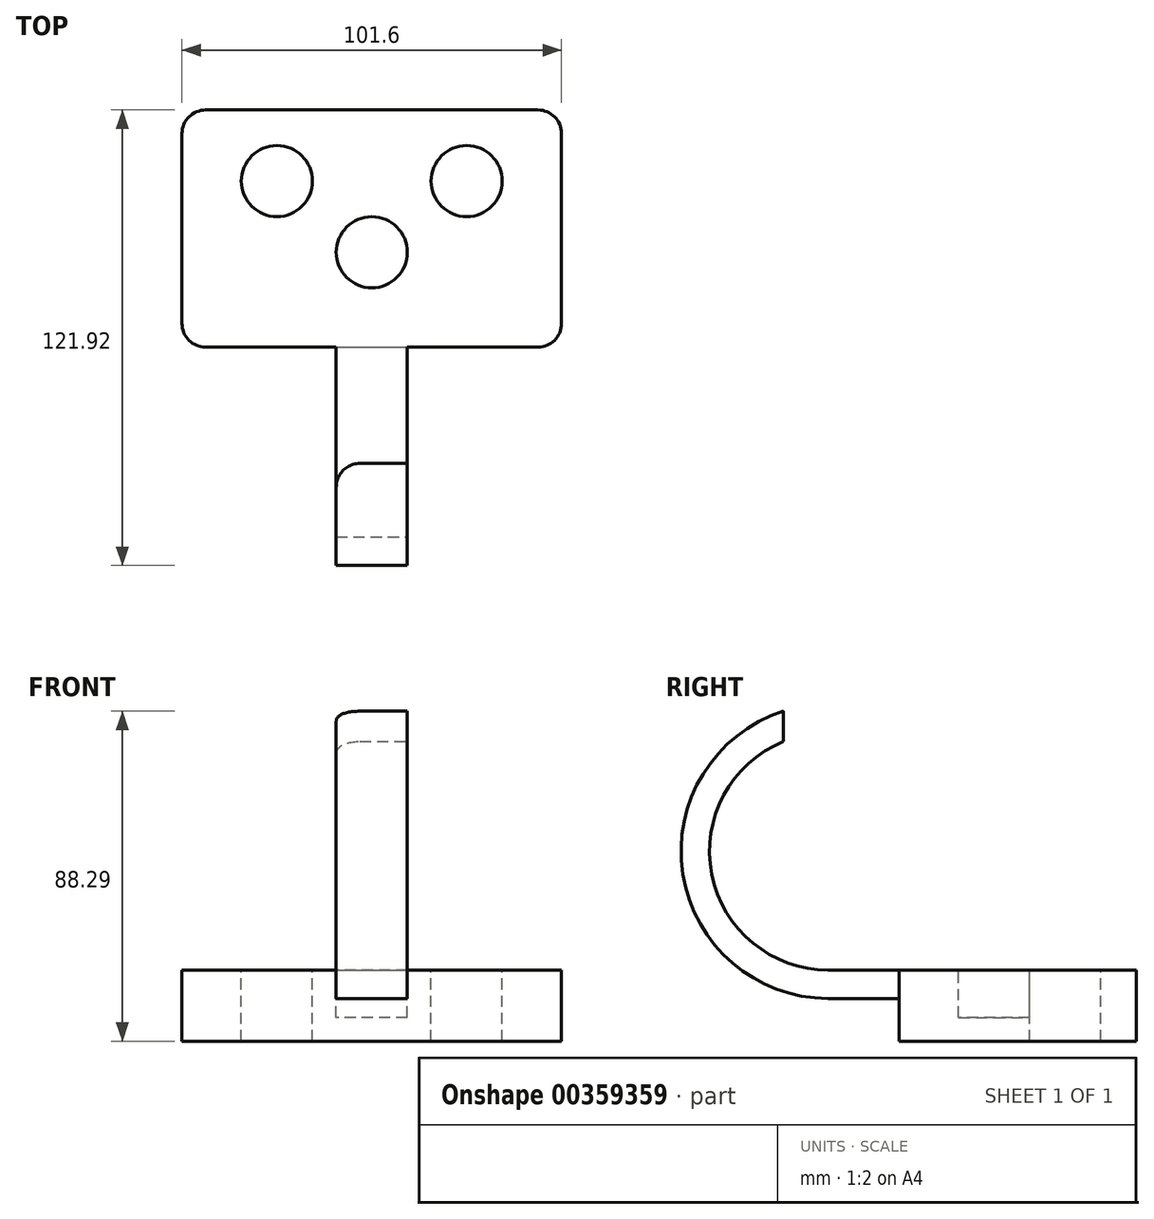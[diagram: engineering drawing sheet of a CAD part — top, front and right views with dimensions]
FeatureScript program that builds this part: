
annotation { "Feature Type Name" : "Feature", "Feature Type Description" : "" }
export const myFeature = defineFeature(function(context is Context, id is Id, definition is map)
    precondition{}
    {
        {
            var Q0;
            Q0=qCreatedBy(makeId("Top.planeOp"),FACE);
            var sketch = newSketch(context, id + "F0", { "sketchPlane" : qUnion([Q0])});
            skLineSegment(sketch, "E0.bottom", {"start": v(0, 0) * mm, "end": v(101.6, 0) * mm});
            skLineSegment(sketch, "E0.top", {"start": v(0, -63.5) * mm, "end": v(101.6, -63.5) * mm});
            skLineSegment(sketch, "E0.left", {"start": v(0, 0) * mm, "end": v(0, -63.5) * mm});
            skLineSegment(sketch, "E0.right", {"start": v(101.6, 0) * mm, "end": v(101.6, -63.5) * mm});
            skSolve(sketch);
        }
        {
            var Q0;
            Q0=makeQuery(id+"F0.imprint","IMPRINT",FACE,{"disambiguationData":[TD([[makeQuery(id+"F0.imprint","IMPRINT",EDGE,{"derivedFrom":sQuery(id+"F0.wireOp",EDGE,"E0.bottom")}),-1.0]])]});
            extrude(context, id + "F1", {"entities" : qUnion([Q0]), "depth" : 19.05 * mm});
        }
        {
            var Q0;
            Q0=makeQuery(id+"F1.opExtrude","SWEPT_EDGE",EDGE,{"disambiguationData":[OSD([sQuery(id+"F0.wireOp",EDGE,"E0.top"),sQuery(id+"F0.wireOp",EDGE,"E0.right")])]});
            var Q1;
            Q1=makeQuery(id+"F1.opExtrude","SWEPT_EDGE",EDGE,{"disambiguationData":[OSD([sQuery(id+"F0.wireOp",EDGE,"E0.bottom"),sQuery(id+"F0.wireOp",EDGE,"E0.right")])]});
            var Q2;
            Q2=makeQuery(id+"F1.opExtrude","SWEPT_EDGE",EDGE,{"disambiguationData":[OSD([sQuery(id+"F0.wireOp",EDGE,"E0.top"),sQuery(id+"F0.wireOp",EDGE,"E0.left")])]});
            var Q3;
            Q3=makeQuery(id+"F1.opExtrude","SWEPT_EDGE",EDGE,{"disambiguationData":[OSD([sQuery(id+"F0.wireOp",EDGE,"E0.bottom"),sQuery(id+"F0.wireOp",EDGE,"E0.left")])]});
            fillet(context, id + "F2", {"entities" : qUnion([Q0, Q1, Q2, Q3]), "radius" : 6.35 * mm, "tangentPropagation" : true, "allowEdgeOverflow" : false});
        }
        {
            var Q0;
            Q0=makeQuery(id+"F1.opExtrude","CAP_FACE",FACE,{"disambiguationData":[OSD([sQuery(id+"F0.wireOp",EDGE,"E0.bottom"),sQuery(id+"F0.wireOp",EDGE,"E0.top"),sQuery(id+"F0.wireOp",EDGE,"E0.left"),sQuery(id+"F0.wireOp",EDGE,"E0.right")])],"isStart":false});
            var sketch = newSketch(context, id + "F3", { "sketchPlane" : qUnion([Q0])});
            skCircle(sketch, "E1", {"center": v(50.8, -38.1) * mm, "radius": 9.53 * mm});
            skPoint(sketch, "E1.centerSnap0", {"position": v(50.8, -63.5) * mm});
            skCircle(sketch, "E2", {"center": v(76.2, -19.05) * mm, "radius": 9.53 * mm});
            skCircle(sketch, "E3", {"center": v(25.4, -19.05) * mm, "radius": 9.53 * mm});
            skSolve(sketch);
        }
        {
            var Q0;
            Q0=makeQuery(id+"F3.imprint","IMPRINT",FACE,{"disambiguationData":[TD([[makeQuery(id+"F3.imprint","IMPRINT",EDGE,{"derivedFrom":sQuery(id+"F3.wireOp",EDGE,"E1")}),1.0]])]});
            extrude(context, id + "F4", {"entities" : qUnion([Q0]), "operationType" : NewBodyOperationType.REMOVE, "oppositeDirection" : true, "depth" : 12.7 * mm});
        }
        {
            var Q0;
            Q0=makeQuery(id+"F3.imprint","IMPRINT",FACE,{"disambiguationData":[TD([[makeQuery(id+"F3.imprint","IMPRINT",EDGE,{"derivedFrom":sQuery(id+"F3.wireOp",EDGE,"E3")}),1.0]])]});
            var Q1;
            Q1=makeQuery(id+"F3.imprint","IMPRINT",FACE,{"disambiguationData":[TD([[makeQuery(id+"F3.imprint","IMPRINT",EDGE,{"derivedFrom":sQuery(id+"F3.wireOp",EDGE,"E2")}),1.0]])]});
            extrude(context, id + "F5", {"entities" : qUnion([Q0, Q1]), "operationType" : NewBodyOperationType.REMOVE, "endBound" : BoundingType.THROUGH_ALL, "oppositeDirection" : true, "depth" : 25.4 * mm});
        }
        {
            var Q0;
            Q0=makeQuery(id+"F1.opExtrude","SWEPT_FACE",FACE,{"disambiguationData":[OSD([sQuery(id+"F0.wireOp",EDGE,"E0.top")])]});
            var sketch = newSketch(context, id + "F6", { "sketchPlane" : qUnion([Q0])});
            skLineSegment(sketch, "E4.bottom", {"start": v(41.28, 19.05) * mm, "end": v(60.33, 19.05) * mm});
            skLineSegment(sketch, "E4.top", {"start": v(41.28, 11.43) * mm, "end": v(60.33, 11.43) * mm});
            skLineSegment(sketch, "E4.left", {"start": v(41.28, 19.05) * mm, "end": v(41.28, 11.43) * mm});
            skLineSegment(sketch, "E4.right", {"start": v(60.33, 19.05) * mm, "end": v(60.33, 11.43) * mm});
            skSolve(sketch);
        }
        {
            var Q0;
            Q0=makeQuery(id+"F6.imprint","IMPRINT",FACE,{"disambiguationData":[TD([[makeQuery(id+"F6.imprint","IMPRINT",EDGE,{"derivedFrom":sQuery(id+"F6.wireOp",EDGE,"E4.bottom")}),-1.0]])]});
            extrude(context, id + "F7", {"entities" : qUnion([Q0]), "operationType" : NewBodyOperationType.ADD, "depth" : 19.05 * mm});
        }
        {
            var Q0;
            Q0=makeQuery(id+"F7.opExtrude","CAP_FACE",FACE,{"disambiguationData":[OSD([sQuery(id+"F6.wireOp",EDGE,"E4.bottom"),sQuery(id+"F6.wireOp",EDGE,"E4.top"),sQuery(id+"F6.wireOp",EDGE,"E4.left"),sQuery(id+"F6.wireOp",EDGE,"E4.right")])],"isStart":false});
            var sketch = newSketch(context, id + "F8", { "sketchPlane" : qUnion([Q0])});
            skLineSegment(sketch, "E5", {"start": v(60.33, 11.43) * mm, "end": v(41.28, 11.43) * mm});
            skLineSegment(sketch, "E6", {"start": v(41.28, 11.43) * mm, "end": v(41.28, 50.8) * mm});
            skLineSegment(sketch, "E7", {"start": v(60.33, 11.43) * mm, "end": v(60.33, 50.8) * mm});
            skLineSegment(sketch, "E8", {"start": v(41.28, 50.8) * mm, "end": v(60.33, 50.8) * mm});
            skSolve(sketch);
        }
        {
            var Q0;
            {var subQ0=sQuery(id+"F8.wireOp",EDGE,"E5");Q0=makeQuery(id+"F8.imprint","IMPRINT",FACE,{"disambiguationData":[TD([[makeQuery(id+"F8.imprint","IMPRINT",EDGE,{"derivedFrom":subQ0}),1.0]])]});}
            var Q1;
            Q1=sQuery(id+"F8.wireOp",EDGE,"E8");
            revolve(context, id + "F9", {"operationType" : NewBodyOperationType.ADD, "entities" : qUnion([Q0]), "axis" : qUnion([Q1]), "revolveType" : RevolveType.ONE_DIRECTION, "oppositeDirection" : true, "angle" : 162.2 * degree});
        }
        {
            var Q0;
            Q0=makeQuery(id+"F9.boolean.opBoolean","MERGE",FACE,{"derivedFrom":[makeQuery(id+"F7.opExtrude","SWEPT_FACE",FACE,{"disambiguationData":[OSD([sQuery(id+"F6.wireOp",EDGE,"E4.right")])]}),makeQuery(id+"F9.opRevolve","SWEPT_FACE",FACE,{"disambiguationData":[OSD([sQuery(id+"F8.wireOp",EDGE,"E7")])]})]});
            var sketch = newSketch(context, id + "F10", { "sketchPlane" : qUnion([Q0])});
            skLineSegment(sketch, "E9", {"start": v(-63.5, 19.05) * mm, "end": v(-63.5, 108.53) * mm});
            skPoint(sketch, "E10", {"position": v(-63.5, 88.29) * mm});
            skLineSegment(sketch, "E11", {"start": v(-63.5, 88.29) * mm, "end": v(-94.58, 88.29) * mm});
            skLineSegment(sketch, "E12.bottom", {"start": v(-94.58, 88.29) * mm, "end": v(-86.64, 88.29) * mm});
            skLineSegment(sketch, "E12.top", {"start": v(-94.58, 76.67) * mm, "end": v(-86.64, 76.67) * mm});
            skLineSegment(sketch, "E12.left", {"start": v(-94.58, 88.29) * mm, "end": v(-94.58, 76.67) * mm});
            skLineSegment(sketch, "E12.right", {"start": v(-86.64, 88.29) * mm, "end": v(-86.64, 76.67) * mm});
            skSolve(sketch);
        }
        {
            var Q0;
            {var subQ1=sQuery(id+"F8.wireOp",EDGE,"E7");var subQ2=makeQuery(id+"F9.opRevolve","CAP_EDGE",EDGE,{"disambiguationData":[OSD([subQ1])],"isStart":false});Q0=makeQuery(id+"F10.imprint","IMPRINT",FACE,{"disambiguationData":[TD([[makeQuery(id+"F10.imprint","IMPRINT",EDGE,{"derivedFrom":subQ2}),1.0]])]});}
            var Q1;
            Q1=makeQuery(id+"F10.imprint","IMPRINT",FACE,{"disambiguationData":[TD([[makeQuery(id+"F10.imprint","IMPRINT",EDGE,{"derivedFrom":sQuery(id+"F10.wireOp",EDGE,"E12.bottom")}),-1.0]])]});
            extrude(context, id + "F11", {"entities" : qUnion([Q0, Q1]), "operationType" : NewBodyOperationType.REMOVE, "oppositeDirection" : true, "depth" : 25.4 * mm});
        }
        {
            var Q0;
            Q0=makeQuery(id+"F11.boolean.opBoolean","COPY",EDGE,{"derivedFrom":makeQuery(id+"F11.opExtrude","CAP_EDGE",EDGE,{"disambiguationData":[OSD([sQuery(id+"F10.wireOp",EDGE,"E12.left")])],"isStart":true})});
            var Q1;
            Q1=makeQuery(id+"F11.boolean.opBoolean","INTERSECT",EDGE,{"derivedFrom":[makeQuery(id+"F9.boolean.opBoolean","MERGE",FACE,{"derivedFrom":[makeQuery(id+"F7.opExtrude","SWEPT_FACE",FACE,{"disambiguationData":[OSD([sQuery(id+"F6.wireOp",EDGE,"E4.left")])]}),makeQuery(id+"F9.opRevolve","SWEPT_FACE",FACE,{"disambiguationData":[OSD([sQuery(id+"F8.wireOp",EDGE,"E6")])]})]}),makeQuery(id+"F11.opExtrude","SWEPT_FACE",FACE,{"disambiguationData":[OSD([sQuery(id+"F10.wireOp",EDGE,"E12.left")])]})]});
            fillet(context, id + "F12", {"entities" : qUnion([Q0, Q1]), "radius" : 6.35 * mm, "tangentPropagation" : true, "allowEdgeOverflow" : false});
        }
    });
